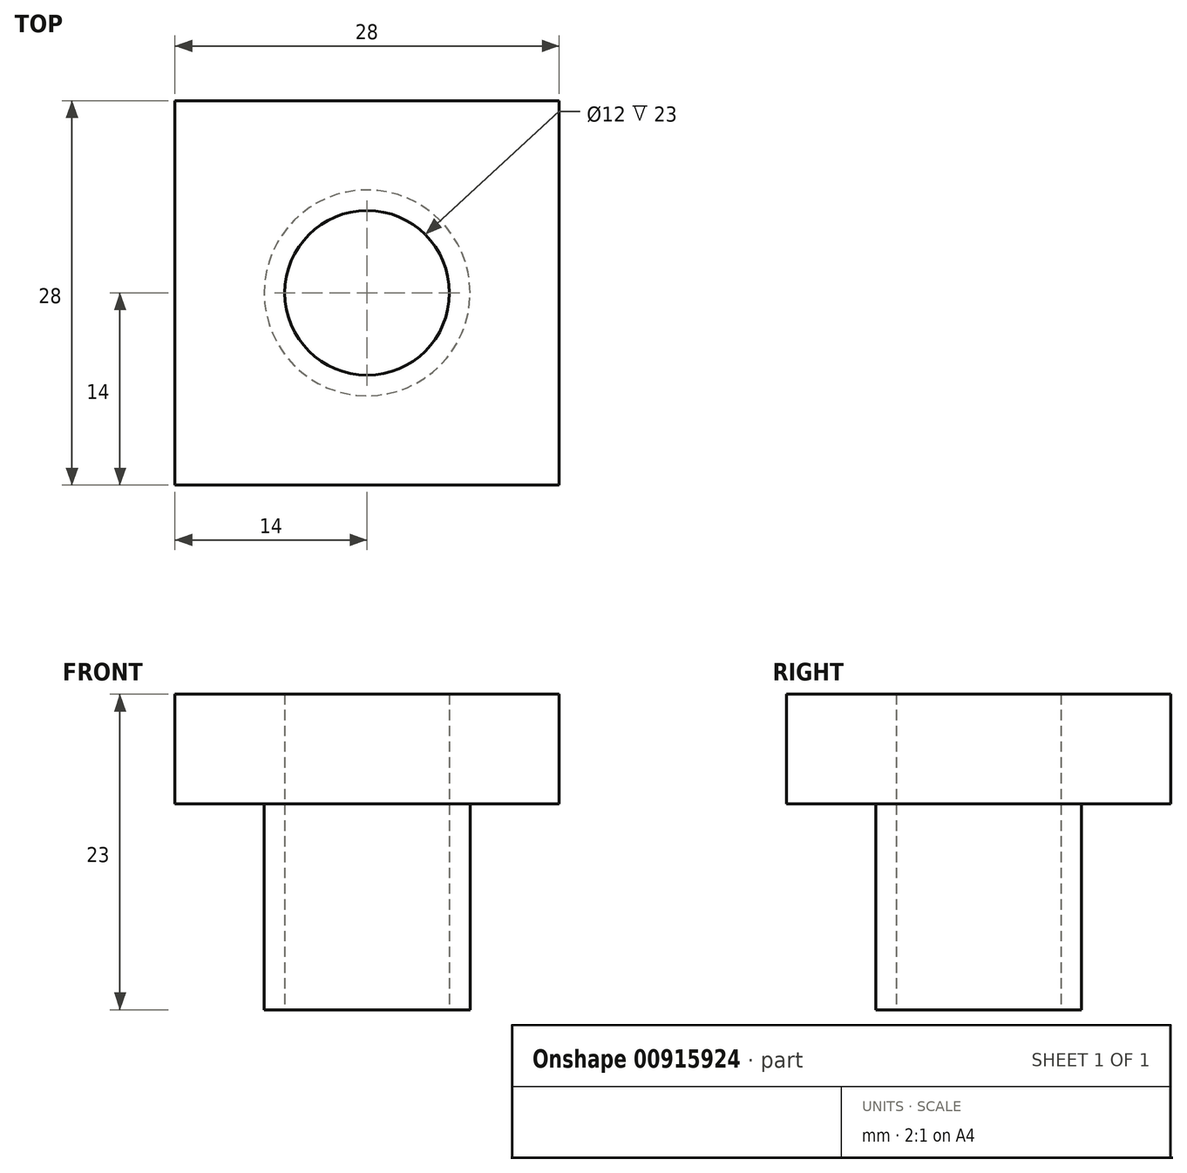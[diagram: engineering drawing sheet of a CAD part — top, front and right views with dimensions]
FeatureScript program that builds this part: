
annotation { "Feature Type Name" : "Feature", "Feature Type Description" : "" }
export const myFeature = defineFeature(function(context is Context, id is Id, definition is map)
    precondition{}
    {
        {
            var Q0;
            Q0=qCreatedBy(makeId("Top.planeOp"),FACE);
            var sketch = newSketch(context, id + "F0", { "sketchPlane" : qUnion([Q0])});
            skLineSegment(sketch, "E0.bottom", {"start": v(14, 14) * mm, "end": v(-14, 14) * mm});
            skLineSegment(sketch, "E0.top", {"start": v(14, -14) * mm, "end": v(-14, -14) * mm});
            skLineSegment(sketch, "E0.left", {"start": v(14, 14) * mm, "end": v(14, -14) * mm});
            skLineSegment(sketch, "E0.right", {"start": v(-14, 14) * mm, "end": v(-14, -14) * mm});
            skPoint(sketch, "E0.middle", {"position": v(0, 0) * mm});
            skSolve(sketch);
        }
        {
            var Q0;
            Q0=makeQuery(id+"F0.imprint","IMPRINT",FACE,{"disambiguationData":[TD([[makeQuery(id+"F0.imprint","IMPRINT",EDGE,{"derivedFrom":sQuery(id+"F0.wireOp",EDGE,"E0.bottom")}),1.0]])]});
            extrude(context, id + "F1", {"entities" : qUnion([Q0]), "depth" : 8 * mm, "offsetDistance" : 25 * mm});
        }
        {
            var Q0;
            Q0=makeQuery(id+"F1.opExtrude","CAP_FACE",FACE,{"disambiguationData":[OSD([sQuery(id+"F0.wireOp",EDGE,"E0.bottom"),sQuery(id+"F0.wireOp",EDGE,"E0.top"),sQuery(id+"F0.wireOp",EDGE,"E0.left"),sQuery(id+"F0.wireOp",EDGE,"E0.right")])],"isStart":true});
            var sketch = newSketch(context, id + "F2", { "sketchPlane" : qUnion([Q0])});
            skCircle(sketch, "E1", {"center": v(0, 0) * mm, "radius": 7.5 * mm});
            skSolve(sketch);
        }
        {
            var Q0;
            Q0 = qSketchRegion(id + "F2", true);
            extrude(context, id + "F3", {"entities" : qUnion([Q0]), "operationType" : NewBodyOperationType.ADD, "depth" : 15 * mm, "offsetDistance" : 25 * mm});
        }
        {
            var Q0;
            Q0=makeQuery(id+"F3.opExtrude","CAP_FACE",FACE,{"disambiguationData":[OSD([sQuery(id+"F2.wireOp",EDGE,"E1")])],"isStart":false});
            var sketch = newSketch(context, id + "F4", { "sketchPlane" : qUnion([Q0])});
            skCircle(sketch, "E2", {"center": v(0, 0) * mm, "radius": 6 * mm});
            skSolve(sketch);
        }
        {
            var Q0;
            Q0=makeQuery(id+"F4.imprint","IMPRINT",FACE,{"disambiguationData":[TD([[makeQuery(id+"F4.imprint","IMPRINT",EDGE,{"derivedFrom":sQuery(id+"F4.wireOp",EDGE,"E2")}),1.0]])]});
            extrude(context, id + "F5", {"entities" : qUnion([Q0]), "operationType" : NewBodyOperationType.REMOVE, "endBound" : BoundingType.THROUGH_ALL, "oppositeDirection" : true, "depth" : 25 * mm, "offsetDistance" : 25 * mm});
        }
    });
